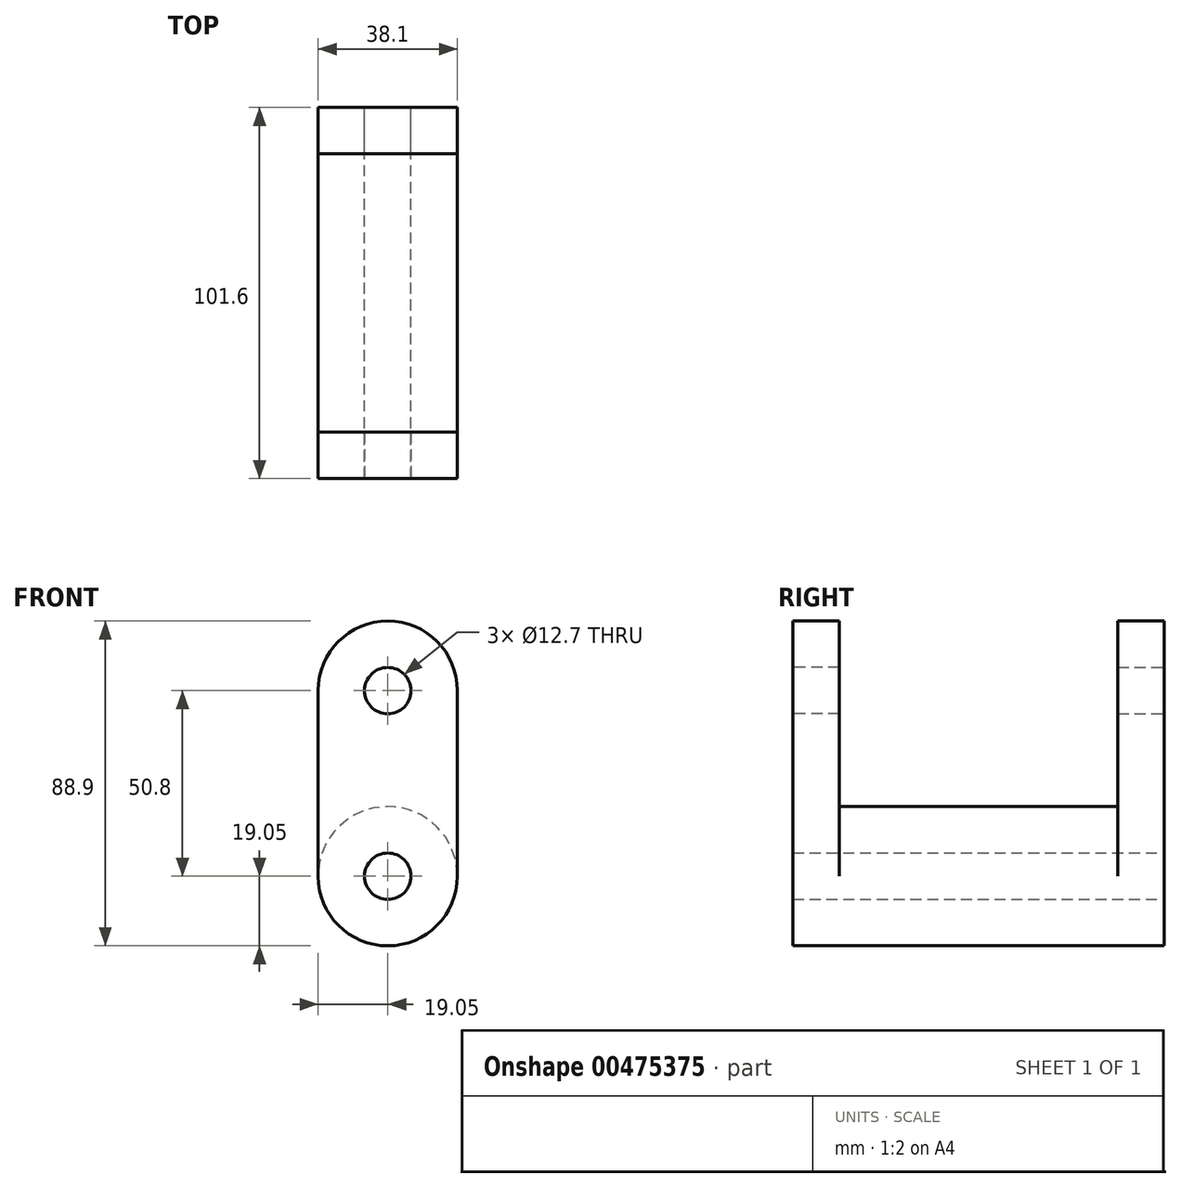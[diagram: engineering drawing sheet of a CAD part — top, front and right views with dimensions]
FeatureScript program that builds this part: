
annotation { "Feature Type Name" : "Feature", "Feature Type Description" : "" }
export const myFeature = defineFeature(function(context is Context, id is Id, definition is map)
    precondition{}
    {
        {
            var Q0;
            Q0=qCreatedBy(makeId("Front.planeOp"),FACE);
            var sketch = newSketch(context, id + "F0", { "sketchPlane" : qUnion([Q0])});
            skCircle(sketch, "E0", {"center": v(0, 0) * mm, "radius": 19.05 * mm});
            skCircle(sketch, "E1", {"center": v(0, 0) * mm, "radius": 6.35 * mm});
            skSolve(sketch);
        }
        {
            var Q0;
            Q0=makeQuery(id+"F0.imprint","IMPRINT",FACE,{"disambiguationData":[TD([[makeQuery(id+"F0.imprint","IMPRINT",EDGE,{"derivedFrom":sQuery(id+"F0.wireOp",EDGE,"E0")}),1.0]])]});
            extrude(context, id + "F1", {"entities" : qUnion([Q0]), "endBound" : BoundingType.SYMMETRIC, "depth" : 101.6 * mm});
        }
        {
            var Q0;
            Q0=makeQuery(id+"F1.opExtrude","CAP_FACE",FACE,{"disambiguationData":[OSD([sQuery(id+"F0.wireOp",EDGE,"E0"),sQuery(id+"F0.wireOp",EDGE,"E1")])],"isStart":false});
            var sketch = newSketch(context, id + "F2", { "sketchPlane" : qUnion([Q0])});
            skLineSegment(sketch, "E2", {"start": v(-19.05, 0) * mm, "end": v(-19.05, 50.8) * mm});
            skLineSegment(sketch, "E3", {"start": v(-19.05, 50.8) * mm, "end": v(19.05, 50.8) * mm});
            skLineSegment(sketch, "E4", {"start": v(19.05, 50.8) * mm, "end": v(19.05, 0) * mm});
            skCircle(sketch, "E5", {"center": v(0, 50.8) * mm, "radius": 19.05 * mm});
            skCircle(sketch, "E6", {"center": v(0, 50.8) * mm, "radius": 6.35 * mm});
            skSolve(sketch);
        }
        {
            var Q0;
            {var subQ0=sQuery(id+"F2.wireOp",EDGE,"E2");Q0=makeQuery(id+"F2.imprint","IMPRINT",FACE,{"disambiguationData":[TD([[makeQuery(id+"F2.imprint","IMPRINT",EDGE,{"derivedFrom":subQ0}),-1.0]])]});}
            var Q1;
            {var subQ1=sQuery(id+"F2.wireOp",EDGE,"E3");var subQ3=sQuery(id+"F2.wireOp",EDGE,"E6");var subQ4=makeQuery(id+"F2.imprint","INTERSECT",VERTEX,{"disambiguationData":[OD(0.0)],"derivedFrom":[subQ1,subQ3]});Q1=makeQuery(id+"F2.imprint","IMPRINT",FACE,{"disambiguationData":[TD([[makeQuery(id+"F2.imprint","IMPRINT",EDGE,{"disambiguationData":[TD([[subQ4,-1.0]])],"derivedFrom":subQ3}),-1.0]])]});}
            var Q2;
            {var subQ1=sQuery(id+"F2.wireOp",EDGE,"E3");var subQ3=sQuery(id+"F2.wireOp",EDGE,"E6");var subQ4=makeQuery(id+"F2.imprint","INTERSECT",VERTEX,{"disambiguationData":[OD(0.0)],"derivedFrom":[subQ1,subQ3]});Q2=makeQuery(id+"F2.imprint","IMPRINT",FACE,{"disambiguationData":[TD([[makeQuery(id+"F2.imprint","IMPRINT",EDGE,{"disambiguationData":[TD([[subQ4,1.0]])],"derivedFrom":subQ3}),-1.0]])]});}
            extrude(context, id + "F3", {"entities" : qUnion([Q0, Q1, Q2]), "operationType" : NewBodyOperationType.ADD, "oppositeDirection" : true, "depth" : 12.7 * mm});
        }
        {
            var Q0;
            Q0=makeQuery(id+"F1.opExtrude","SWEPT_BODY",BODY,{"disambiguationData":[OSD([sQuery(id+"F0.wireOp",EDGE,"E0"),sQuery(id+"F0.wireOp",EDGE,"E1")])]});
            var Q1;
            Q1=qCreatedBy(makeId("Front.planeOp"),FACE);
            mirror(context, id + "F4", {"operationType" : NewBodyOperationType.ADD, "entities" : qUnion([Q0]), "mirrorPlane" : qUnion([Q1])});
        }
    });
